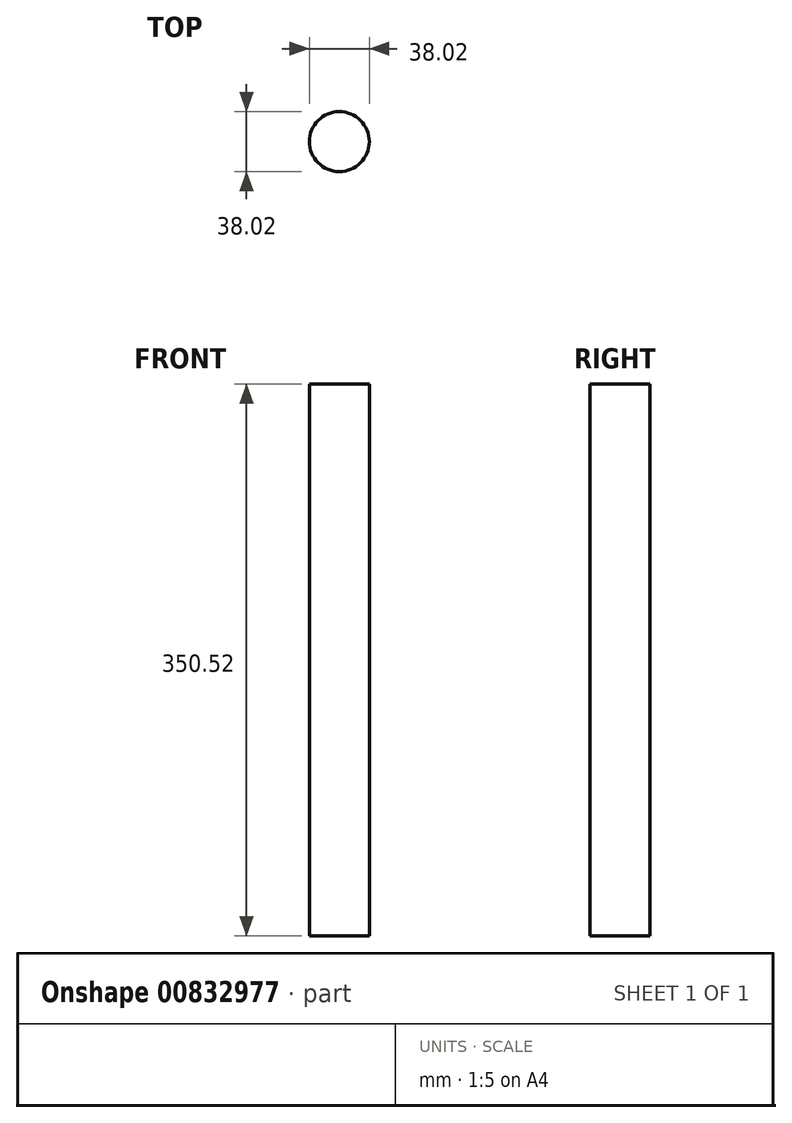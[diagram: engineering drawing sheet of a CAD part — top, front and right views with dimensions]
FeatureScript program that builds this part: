
annotation { "Feature Type Name" : "Feature", "Feature Type Description" : "" }
export const myFeature = defineFeature(function(context is Context, id is Id, definition is map)
    precondition{}
    {
        {
            var Q0;
            Q0=qCreatedBy(makeId("Top.planeOp"),FACE);
            var sketch = newSketch(context, id + "F0", { "sketchPlane" : qUnion([Q0])});
            skCircle(sketch, "E0", {"center": v(0, 0) * mm, "radius": 19 * mm});
            skSolve(sketch);
        }
        {
            var Q0;
            Q0 = qSketchRegion(id + "F0", true);
            extrude(context, id + "F1", {"entities" : qUnion([Q0]), "depth" : 350.52 * mm, "offsetDistance" : 25.4 * mm});
        }
    });
